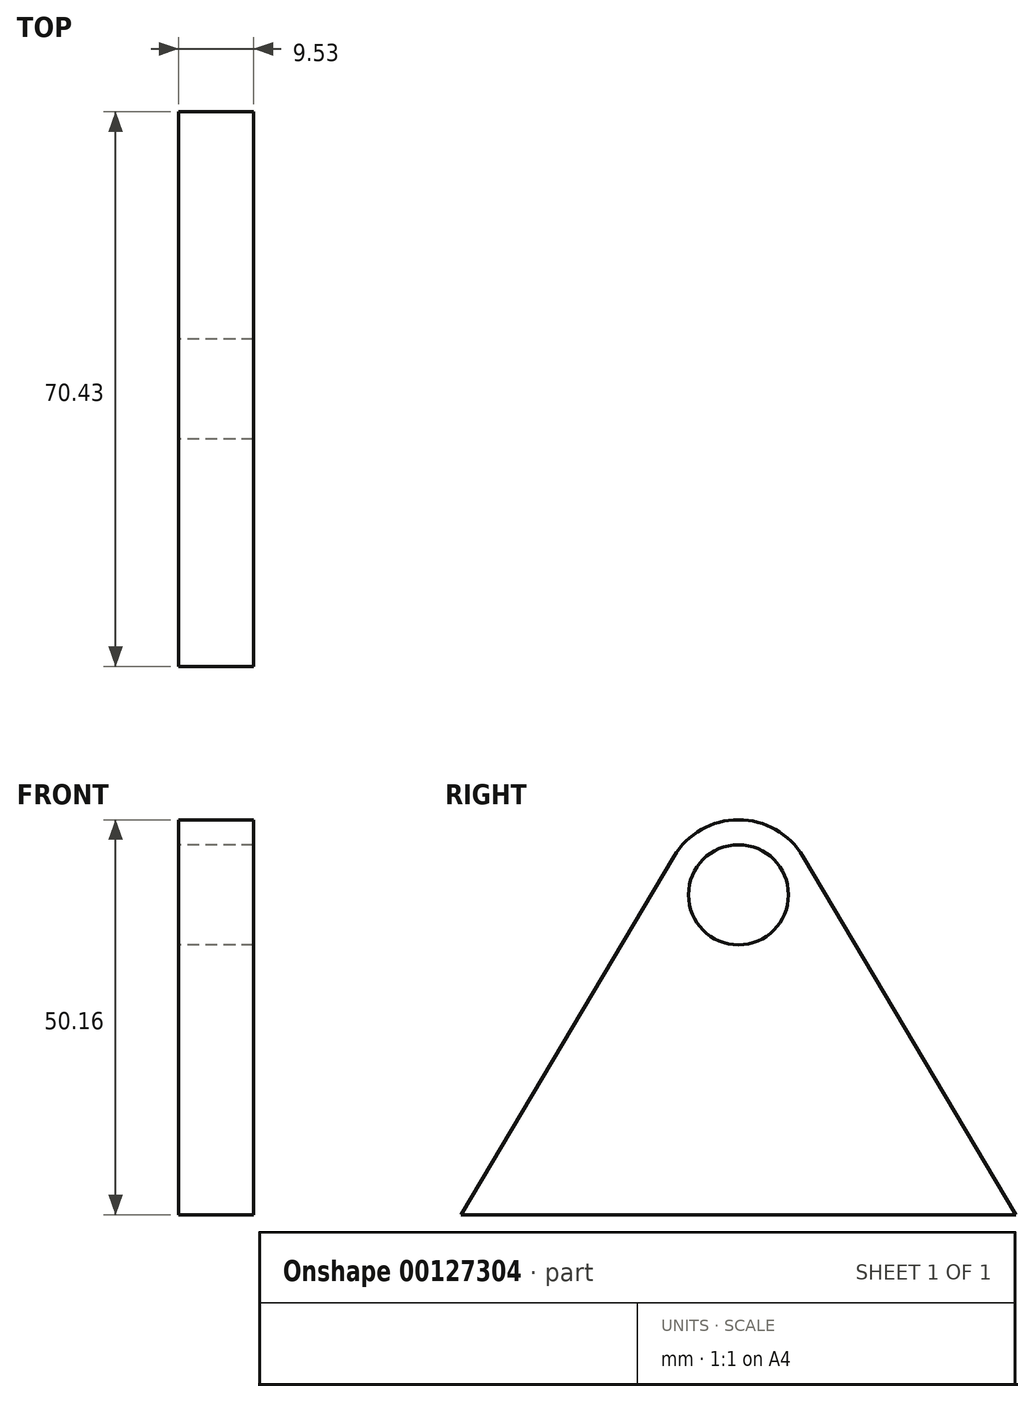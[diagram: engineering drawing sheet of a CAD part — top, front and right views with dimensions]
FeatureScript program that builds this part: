
annotation { "Feature Type Name" : "Feature", "Feature Type Description" : "" }
export const myFeature = defineFeature(function(context is Context, id is Id, definition is map)
    precondition{}
    {
        {
            var Q0;
            Q0=qCreatedBy(makeId("Right.planeOp"),FACE);
            var sketch = newSketch(context, id + "F0", { "sketchPlane" : qUnion([Q0])});
            skLineSegment(sketch, "E0", {"start": v(0, 0) * mm, "end": v(70.43, 0) * mm});
            skCircle(sketch, "E1", {"center": v(35.22, 40.64) * mm, "radius": 6.35 * mm});
            skArc(sketch, "E2", {"start": v(43.4, 45.5) * mm, "mid": v(35.22, 50.17) * mm, "end": v(27.03, 45.5) * mm});
            skLineSegment(sketch, "E3", {"start": v(0, 0) * mm, "end": v(27.03, 45.5) * mm});
            skLineSegment(sketch, "E4", {"start": v(70.43, 0) * mm, "end": v(43.4, 45.5) * mm});
            skLineSegment(sketch, "E5", {"start": v(35.22, 0) * mm, "end": v(35.22, 52.73) * mm, "construction": true});
            skSolve(sketch);
        }
        {
            var Q0;
            Q0 = qSketchRegion(id + "F0", true);
            extrude(context, id + "F1", {"entities" : qUnion([Q0]), "depth" : 9.52 * mm});
        }
    });
